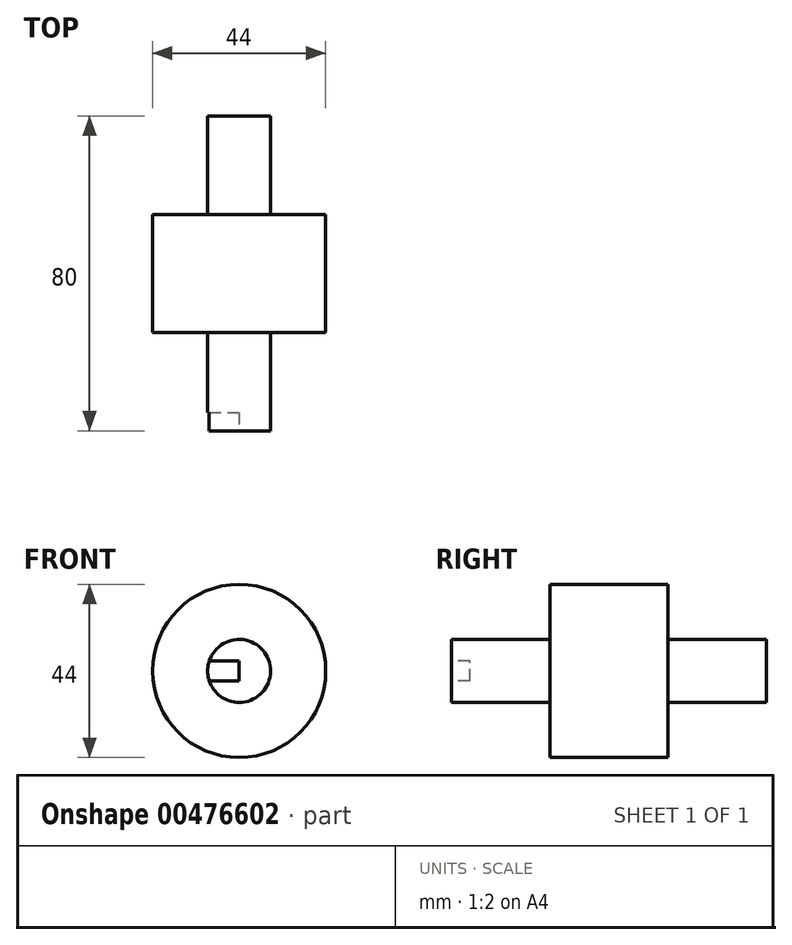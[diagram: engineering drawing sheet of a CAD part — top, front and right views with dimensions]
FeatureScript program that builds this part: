
annotation { "Feature Type Name" : "Feature", "Feature Type Description" : "" }
export const myFeature = defineFeature(function(context is Context, id is Id, definition is map)
    precondition{}
    {
        {
            var Q0;
            Q0=qCreatedBy(makeId("Right.planeOp"),FACE);
            var sketch = newSketch(context, id + "F0", { "sketchPlane" : qUnion([Q0])});
            skLineSegment(sketch, "E0", {"start": v(-61.18, 0) * mm, "end": v(90.72, 0) * mm, "construction": true});
            skLineSegment(sketch, "E1", {"start": v(-40, 0) * mm, "end": v(-40, 8) * mm});
            skLineSegment(sketch, "E2", {"start": v(-40, 8) * mm, "end": v(-15, 8) * mm});
            skLineSegment(sketch, "E3", {"start": v(-15, 8) * mm, "end": v(-15, 22) * mm});
            skLineSegment(sketch, "E4", {"start": v(-15, 22) * mm, "end": v(15, 22) * mm});
            skLineSegment(sketch, "E5", {"start": v(15, 22) * mm, "end": v(15, 8) * mm});
            skLineSegment(sketch, "E6", {"start": v(15, 8) * mm, "end": v(40, 8) * mm});
            skLineSegment(sketch, "E7", {"start": v(40, 8) * mm, "end": v(40, 0) * mm});
            skLineSegment(sketch, "E8", {"start": v(40, 0) * mm, "end": v(-40, 0) * mm});
            skSolve(sketch);
        }
        {
            var Q0;
            Q0=makeQuery(id+"F0.imprint","IMPRINT",FACE,{"disambiguationData":[TD([[makeQuery(id+"F0.imprint","IMPRINT",EDGE,{"derivedFrom":sQuery(id+"F0.wireOp",EDGE,"E1")}),-1.0]])]});
            var Q1;
            Q1=sQuery(id+"F0.wireOp",EDGE,"E0");
            revolve(context, id + "F1", {"entities" : qUnion([Q0]), "axis" : qUnion([Q1]), "revolveType" : RevolveType.FULL});
        }
        {
            var Q0;
            Q0=qCreatedBy(makeId("Right.planeOp"),FACE);
            var sketch = newSketch(context, id + "F2", { "sketchPlane" : qUnion([Q0])});
            skLineSegment(sketch, "E9.bottom", {"start": v(-35.37, -2.5) * mm, "end": v(-45.27, -2.5) * mm});
            skLineSegment(sketch, "E9.top", {"start": v(-35.37, 2.5) * mm, "end": v(-45.27, 2.5) * mm});
            skLineSegment(sketch, "E9.left", {"start": v(-35.37, -2.5) * mm, "end": v(-35.37, 2.5) * mm});
            skLineSegment(sketch, "E9.right", {"start": v(-45.27, -2.5) * mm, "end": v(-45.27, 2.5) * mm});
            skSolve(sketch);
        }
        {
            var Q0;
            Q0 = qSketchRegion(id + "F2", true);
            extrude(context, id + "F3", {"entities" : qUnion([Q0]), "operationType" : NewBodyOperationType.REMOVE, "endBound" : BoundingType.THROUGH_ALL, "oppositeDirection" : true, "depth" : 25 * mm});
        }
    });
